# Revit family: GRANIT_8
name_source: partatom
category: Drzwi
revit_build: Autodesk Revit 2016 (Build: 20150714_1515(x64)
units: mm (PartAtom-declared; Revit-internal decimal feet)

## family parameters
Obiekt nadrzędny = Ściana
Punkt obliczania pomieszczeń = Nie
Tnij formami wycięć po wczytaniu = Nie
Współdzielony = Nie
Zawsze pionowo = Tak

## types (8) — shared parameters
Funkcja = Wewnętrzna
Informacja = Własność Porta KMI Poland, wszelkie prawa zastrzeżone.
Konstrukcja analityczna = <Brak>
Odwzorowanie ramy - wewnętrzne = 25 mm  [stored 0.082021 ft]
Odwzorowanie ramy - zewnętrzne = 25 mm  [stored 0.082021 ft]
Producent = PORTA KMI POLAND
Szerokość ramy = 75 mm  [stored 0.246063 ft]
Zakończenie ściany = Wg obiektu nadrzędnego

## per-type parameters (varying)
| type | Opis | SB | Szerokość | URL | Wysokość |
| PN 80 | Biblioteki CAD produktów firmy PORTA KMI POLAND S.A. wraz z ich wizualizacjami są chronione prawami własności przemysłowej i intelektualnej. Można je wykorzystywać do handlowych celów osobistych poprzez zastosowanie w projektach, jednak nie wolno ich powielać, modyfikować, licencjonować ani publikować, w całości ani w części, chyba że celem przeglądania, bez uprzedniej pisemnej zgody PORTA KMI Poland sp.z.o.o. www.porta.com.pl | 856 mm  [stored 2.8084 ft] | 876 mm  [stored 2.87402 ft] | www.porta.com.pl , www.portadoors.com , www.portacad.eu | 2056 mm  [stored 6.74541 ft] |
| PN 90 | Biblioteki CAD produktów firmy PORTA KMI POLAND S.A. wraz z ich wizualizacjami są chronione prawami własności przemysłowej i intelektualnej. Można je wykorzystywać do handlowych celów osobistych poprzez zastosowanie w projektach, jednak nie wolno ich powielać, modyfikować, licencjonować ani publikować, w całości ani w części, chyba że celem przeglądania, bez uprzedniej pisemnej zgody PORTA KMI Poland sp.z.o.o. www.porta.com.pl | 964 mm  [stored 3.16273 ft] | 984 mm  [stored 3.22835 ft] | www.porta.com.pl , www.portadoors.com , www.portacad.eu | 2056 mm  [stored 6.74541 ft] |
| PN 100 |  | 1056 mm  [stored 3.46457 ft] | 1076 mm  [stored 3.53018 ft] | www.porta.com.pl | 2056 mm  [stored 6.74541 ft] |
| C'eska' a Slovenska' 80 |  | 860 mm | 880 mm  [stored 2.88714 ft] | www.porta.com.pl , www.portadoors.com , www.portacad.eu | 2005 mm  [stored 6.57808 ft] |
| C'eska' a Slovenska' 90 |  | 960 mm  [stored 3.14961 ft] | 980 mm  [stored 3.21522 ft] | www.porta.com.pl , www.portadoors.com , www.portacad.eu | 2005 mm  [stored 6.57808 ft] |
| C'eska' a Slovenska' 100 |  | 1060 mm  [stored 3.47769 ft] | 1080 mm  [stored 3.54331 ft] | www.porta.com.pl , www.portadoors.com , www.portacad.eu | 2005 mm  [stored 6.57808 ft] |
| DIN 80 |  | 865 mm  [stored 2.83793 ft] | 885 mm | www.porta.com.pl , www.portadoors.com , www.portacad.eu | 2005 mm  [stored 6.57808 ft] |
| DIN 90 |  | 990 mm  [stored 3.24803 ft] | 1010 mm  [stored 3.31365 ft] | www.porta.com.pl , www.portadoors.com , www.portacad.eu | 2005 mm  [stored 6.57808 ft] |

note: [stored X ft] marks values corroborated as IEEE doubles in the binary element streams (Revit-internal decimal feet)

## geometry (parser evidence)
native form markers: Blend x2, Sweep x3
no freeform markers — native parametric forms only
